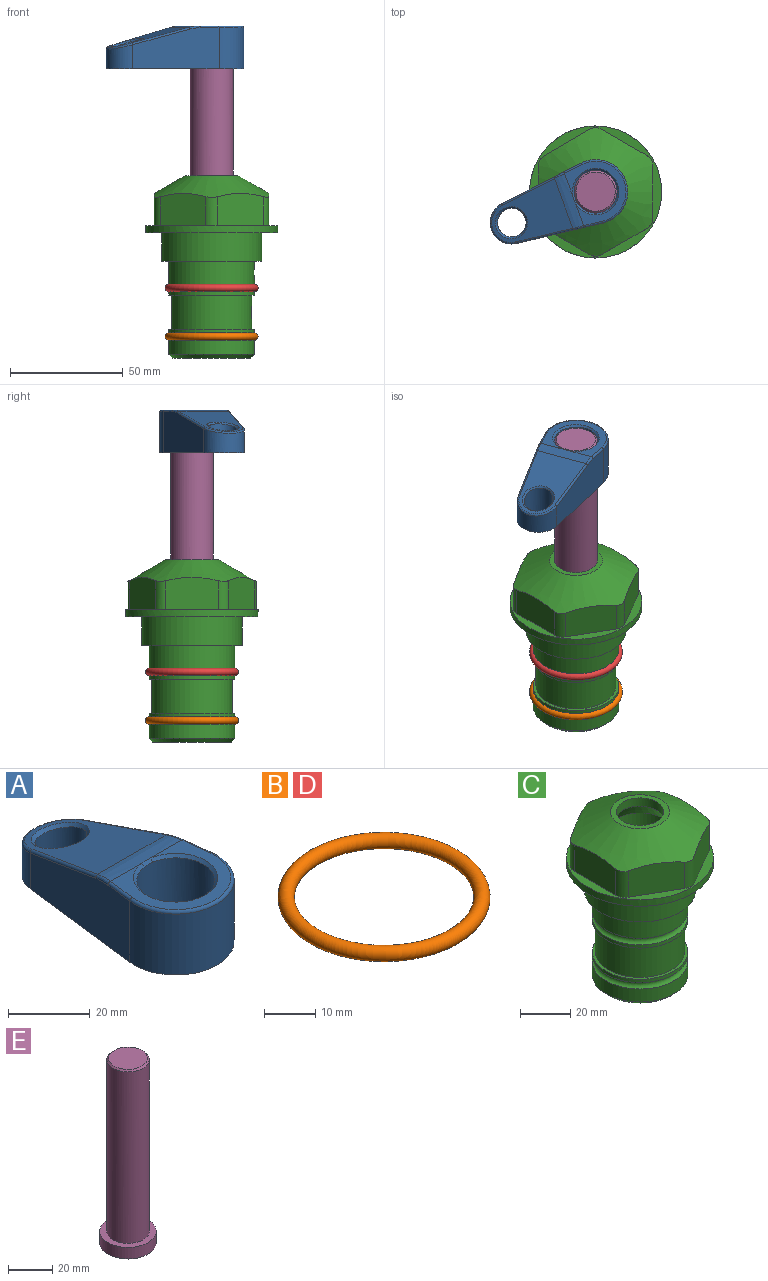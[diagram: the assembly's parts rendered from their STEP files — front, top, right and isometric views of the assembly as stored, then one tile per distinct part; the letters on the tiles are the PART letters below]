
ASSEMBLY  parts=5 mates=4
PART A: 31 faces, bbox 31.7x65.5x19.8 mm
  f0: plane 39.12x18.26mm, normal (0.99,0.12,0), area 612.2mm2, adj f1,f4,f7,f11,f13,f15
  f1: cylinder r=9.53mm len=18.91mm, axis (0,0,-1), area 296.1mm2, adj f0,f2,f7,f17
  f2: plane 39.12x18.26mm, normal (-0.99,0.12,0), area 612.2mm2, adj f1,f4,f7,f12,f14,f16
  f3: cylinder r=6.35mm len=12.7mm, axis (0,0,-1), area 362.4mm2, adj f7,f18
  f4: cylinder r=14.29mm len=28.58mm, axis (0,0,-1), area 882.2mm2, adj f0,f2,f7,f10
  f5: cylinder r=9.53mm len=19.05mm, axis (0,0,-1), area 1092.6mm2, adj f7,f19,f20
  f6: plane 26.99x23.69mm, normal (0,0,1), area 216.2mm2, adj f9,f10,f11,f12,f19
  f7: plane 63.5x28.58mm, normal (0,0,-1), area 661.8mm2, adj f0,f1,f2,f3,f4,f5,f22,f23
  f8: plane 33.52x23.6mm, normal (0,0.26,0.97), area 486mm2, adj f9,f15,f16,f17,f18
  f9: cylinder r=19.05mm len=24.72mm, axis (1,0,0), area 120.4mm2, adj f6,f8,f13,f14,f20
  f10: torus R=13.49mm, axis (0,0,1), area 59mm2, adj f4,f6,f11,f12
  f11: cylinder r=0.79mm len=8.67mm, axis (0.12,-0.99,0), area 10.8mm2, adj f0,f6,f10,f13
  f12: cylinder r=0.79mm len=8.67mm, axis (0.12,0.99,0), area 10.8mm2, adj f2,f6,f10,f14
  f13: bspline ~4.95x1.42mm, area 6.1mm2, adj f0,f9,f11,f15
  f14: bspline ~4.95x1.42mm, area 6.1mm2, adj f2,f9,f12,f16
  f15: cylinder r=0.79mm len=25.95mm, axis (0.12,-0.96,0.26), area 32.9mm2, adj f0,f8,f13,f17
  f16: cylinder r=0.79mm len=25.95mm, axis (0.12,0.96,-0.26), area 32.9mm2, adj f2,f8,f14,f17
  f17: bspline ~18.91x8.38mm, area 30mm2, adj f1,f8,f15,f16
  f18: bspline ~14.29x14.29mm, area 48.3mm2, adj f3,f8
  f19: cone r=9.53mm half-angle=45deg, axis (0,0,1), area 66.5mm2, adj f5,f6,f20
  f20: bspline ~3.22x0.96mm, area 3.5mm2, adj f5,f9,f19
  f21: plane 2.75x2.72mm, normal (0,0,-1), area 2.9mm2, adj f23,f25,f28
  f22: plane 23.05x15.88mm, normal (-0.99,-0.12,0), area 323.6mm2, adj f7,f25,f26,f27,f28,f29
  f23: plane 23.05x15.88mm, normal (0.99,-0.12,0), area 323.6mm2, adj f7,f21,f25,f27,f28,f30
  f24: cylinder r=9.53mm len=10.69mm, axis (0,0,-1), area 114.7mm2, adj f7,f27,f29,f30
  f25: cylinder r=12.7mm len=20.59mm, axis (0,0,-1), area 381.1mm2, adj f7,f21,f22,f23,f26,f28
  f26: plane 2.75x2.72mm, normal (0,0,-1), area 2.9mm2, adj f22,f25,f28
  f27: plane 19.72x18.37mm, normal (0,-0.26,-0.97), area 291.8mm2, adj f22,f23,f24,f28,f29,f30
  f28: cylinder r=15.88mm len=19.92mm, axis (1,0,0), area 54.8mm2, adj f21,f22,f23,f25,f26,f27
  f29: cylinder r=1.59mm len=11mm, axis (0,0,-1), area 34.7mm2, adj f7,f22,f24,f27
  f30: cylinder r=1.59mm len=11mm, axis (0,0,-1), area 34.7mm2, adj f7,f23,f24,f27
PART B: 1 faces, bbox 44.7x44.7x3.2 mm
  f0: torus R=19.05mm, axis (0,0,1), area 1193.9mm2
PART C: 36 faces, bbox 58.7x58.7x81 mm
  f0: cylinder r=17.78mm len=35.56mm, axis (0,0,1), area 1670.8mm2, adj f23,f24,f31
  f1: cylinder r=19.05mm len=38.1mm, axis (0,0,1), area 1191.9mm2, adj f26,f27,f30
  f2: plane 58.66x58.66mm, normal (0,0,-1), area 1150.6mm2, adj f3,f28
  f3: cylinder r=29.33mm len=58.66mm, axis (0,0,-1), area 585.1mm2, adj f2,f4
  f4: plane 58.66x58.66mm, normal (0,0,1), area 475.9mm2, adj f3,f5,f6,f7,f8,f9,f10,f11
  f5: plane 20.32x14.34mm, normal (-0.5,0.87,0), area 324.4mm2, adj f4,f15,f16,f17
  f6: plane 20.32x14.34mm, normal (0.5,0.87,0), area 324.4mm2, adj f4,f14,f15,f17
  f7: plane 23.48x14.34mm, normal (1,0,0), area 324.4mm2, adj f4,f13,f14,f17
  f8: plane 20.32x14.34mm, normal (0.5,-0.87,0), area 324.4mm2, adj f4,f12,f13,f17
  f9: plane 20.32x14.34mm, normal (-0.5,-0.87,0), area 324.4mm2, adj f4,f11,f12,f17
  f10: plane 23.48x14.34mm, normal (-1,0,0), area 324.4mm2, adj f4,f11,f16,f17
  f11: cylinder r=5.08mm len=12.85mm, axis (0,0,-1), area 67.2mm2, adj f4,f9,f10,f17
  f12: cylinder r=5.08mm len=12.85mm, axis (0,0,-1), area 67.2mm2, adj f4,f8,f9,f17
  f13: cylinder r=5.08mm len=12.85mm, axis (0,0,-1), area 67.2mm2, adj f4,f7,f8,f17
  f14: cylinder r=5.08mm len=12.85mm, axis (0,0,-1), area 67.2mm2, adj f4,f6,f7,f17
  f15: cylinder r=5.08mm len=12.85mm, axis (0,0,-1), area 67.2mm2, adj f4,f5,f6,f17
  f16: cylinder r=5.08mm len=12.85mm, axis (0,0,-1), area 67.2mm2, adj f4,f5,f10,f17
  f17: cone r=11.73mm half-angle=60deg, axis (0,0,-1), area 2071.8mm2, adj f5,f6,f7,f8,f9,f10,f11,f12
  f18: plane 23.46x23.46mm, normal (0,0,1), area 147.4mm2, adj f17,f35
  f19: plane 34.93x34.93mm, normal (0,0,-1), area 958mm2, adj f29
  f20: cylinder r=19.05mm len=38.1mm, axis (0,0,1), area 760.1mm2, adj f21,f29
  f21: torus R=19.05mm, axis (0,0,1), area 565.3mm2, adj f20,f22
  f22: cylinder r=19.05mm len=38.1mm, axis (0,0,1), area 190mm2, adj f21,f23
  f23: plane 38.1x38.1mm, normal (0,0,1), area 146.9mm2, adj f0,f22
  f24: plane 38.1x38.1mm, normal (0,0,-1), area 146.9mm2, adj f0,f25
  f25: cylinder r=19.05mm len=38.1mm, axis (0,0,1), area 190mm2, adj f24,f26
  f26: torus R=19.05mm, axis (0,0,1), area 565.3mm2, adj f1,f25
  f27: plane 44.45x44.45mm, normal (0,0,-1), area 411.7mm2, adj f1,f28
  f28: cylinder r=22.23mm len=44.45mm, axis (0,0,1), area 1773.5mm2, adj f2,f27
  f29: cone r=19.05mm half-angle=45deg, axis (0,0,1), area 257.5mm2, adj f19,f20
  f30: cylinder r=3.17mm len=6.75mm, axis (-1,0,0), area 128mm2, adj f1,f33
  f31: cylinder r=3.17mm len=6.35mm, axis (-1,0,0), area 102.5mm2, adj f0,f33
  f32: plane 25.4x25.4mm, normal (0,0,1), area 506.7mm2, adj f33
  f33: cylinder r=12.7mm len=66.42mm, axis (0,0,-1), area 5236.2mm2, adj f30,f31,f32,f34
  f34: cone r=9.53mm half-angle=30deg, axis (0,0,-1), area 443.4mm2, adj f33,f35
  f35: cylinder r=9.53mm len=19.05mm, axis (0,0,-1), area 240.9mm2, adj f18,f34
PART D: same geometry as B
PART E: 6 faces, bbox 25.4x25.4x101.6 mm
  f0: plane 17.46x17.46mm, normal (0,0,1), area 239.5mm2, adj f5
  f1: plane 25.4x25.4mm, normal (0,0,-1), area 506.7mm2, adj f2
  f2: cylinder r=12.7mm len=25.4mm, axis (0,0,1), area 506.7mm2, adj f1,f3
  f3: plane 25.4x25.4mm, normal (0,0,1), area 221.7mm2, adj f2,f4
  f4: cylinder r=9.53mm len=94.46mm, axis (0,0,1), area 5653mm2, adj f3,f5
  f5: cone r=8.73mm half-angle=45deg, axis (0,0,-1), area 64.4mm2, adj f0,f4
PLACE A rot(axis=(0,0,1),110.2deg) t=(0,0,28.35)mm
PLACE B t=(0,0,-21.59)mm
PLACE C at identity fixed
PLACE D at identity
PLACE E rot(axis=(0,0,1),110.2deg) t=(0,0,27.55)mm
MATE fastened C.f0 <-> D.f0  axis (0,0,1) through (0,0,-24.51)mm
MATE cylindrical E.f2 <-> C.f0  axis (0,0,-1) through (0,0,-10.55)mm
MATE fastened A.f4 <-> E.f2  axis (0,0,1) through (0,0,91.05)mm
MATE fastened C.f0 <-> B.f0  axis (0,0,1) through (0,0,-46.1)mm
